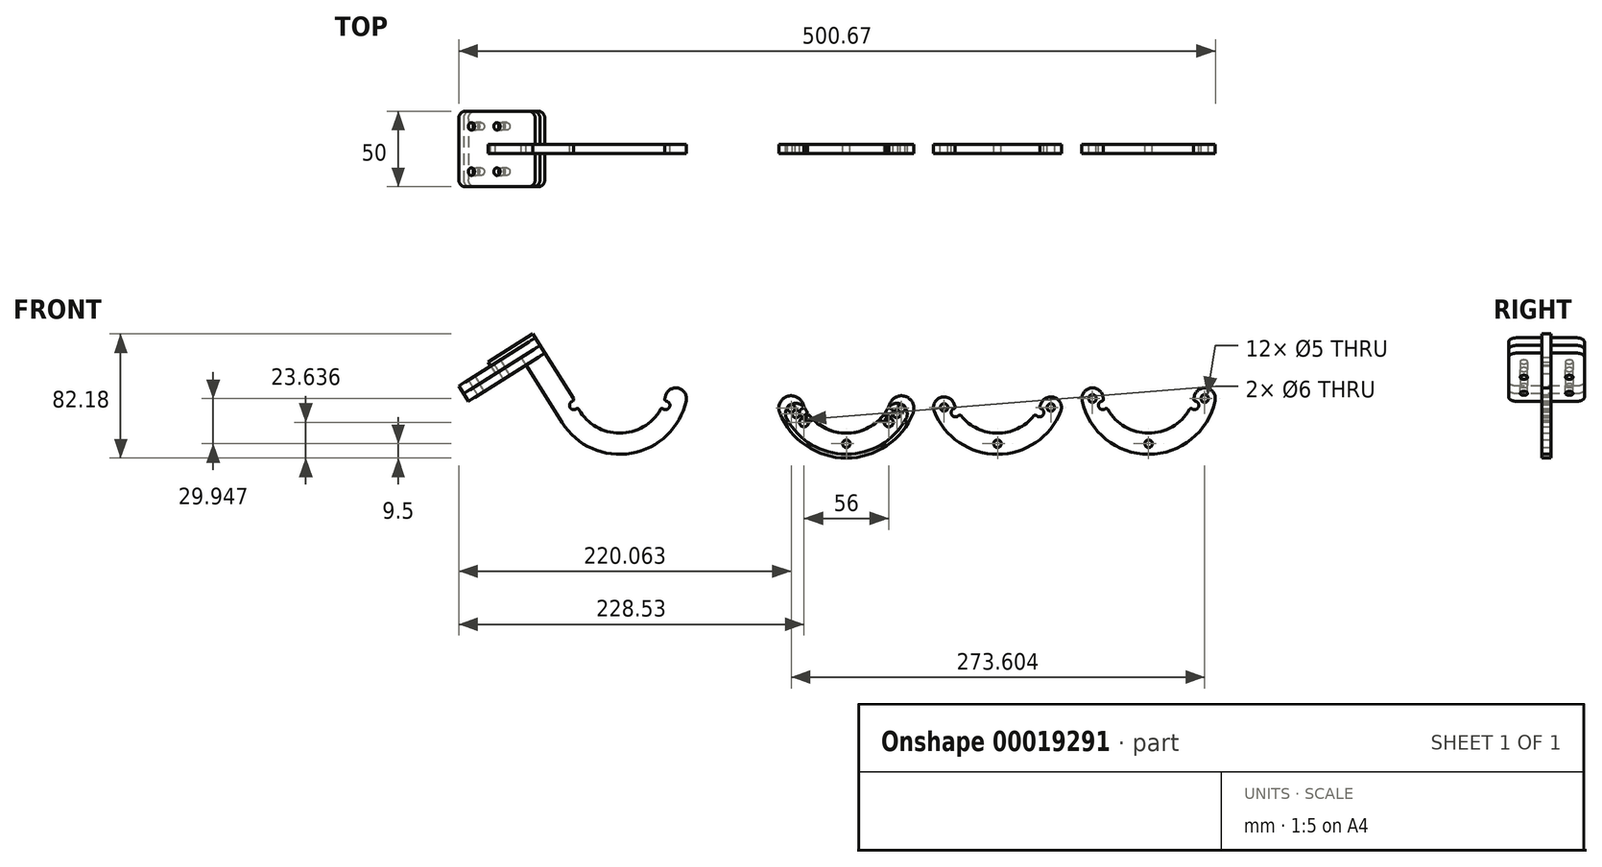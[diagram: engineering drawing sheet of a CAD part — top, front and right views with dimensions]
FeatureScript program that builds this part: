
annotation { "Feature Type Name" : "Feature", "Feature Type Description" : "" }
export const myFeature = defineFeature(function(context is Context, id is Id, definition is map)
    precondition{}
    {
        {
            var Q0;
            Q0=qCreatedBy(makeId("Front.planeOp"),FACE);
            var sketch = newSketch(context, id + "F0", { "sketchPlane" : qUnion([Q0])});
            skCircle(sketch, "E0", {"center": v(0, 0) * mm, "radius": 30 * mm, "construction": true});
            skArc(sketch, "E1", {"start": v(-25.2, -18.05) * mm, "mid": v(-27.55, -22.7) * mm, "end": v(-22.53, -21.3) * mm});
            skArc(sketch, "E2", {"start": v(-22.53, -21.3) * mm, "mid": v(0, -31) * mm, "end": v(22.53, -21.3) * mm});
            skArc(sketch, "E3.trimOffspring", {"start": v(25.2, -18.05) * mm, "mid": v(26.24, -16.5) * mm, "end": v(27.19, -14.9) * mm});
            skArc(sketch, "E4.trimOffspring", {"start": v(22.53, -21.3) * mm, "mid": v(27.55, -22.7) * mm, "end": v(25.2, -18.05) * mm});
            skLineSegment(sketch, "E5", {"start": v(0, -20.9) * mm, "end": v(0, 0) * mm, "construction": true});
            skArc(sketch, "E6.trimOffspring", {"start": v(-27.19, -14.9) * mm, "mid": v(-26.24, -16.5) * mm, "end": v(-25.2, -18.05) * mm});
            skLineSegment(sketch, "E7", {"start": v(-27.19, -14.9) * mm, "end": v(27.19, -14.9) * mm, "construction": true});
            skLineSegment(sketch, "E8", {"start": v(-25.35, -20.9) * mm, "end": v(25.35, -20.9) * mm, "construction": true});
            skArc(sketch, "E9", {"start": v(-39.47, -21.62) * mm, "mid": v(0, -45) * mm, "end": v(39.47, -21.62) * mm});
            skArc(sketch, "E10", {"start": v(-27.19, -14.9) * mm, "mid": v(-36.7, -12.12) * mm, "end": v(-39.47, -21.62) * mm});
            skArc(sketch, "E11.0.MirrorCS", {"start": v(27.19, -14.9) * mm, "mid": v(36.7, -12.12) * mm, "end": v(39.47, -21.62) * mm});
            skCircle(sketch, "E12", {"center": v(-33.33, -18.26) * mm, "radius": 2.5 * mm});
            skCircle(sketch, "E13", {"center": v(-33.33, -18.26) * mm, "radius": 4.5 * mm, "construction": true});
            skCircle(sketch, "E14.0.MirrorC", {"center": v(33.33, -18.26) * mm, "radius": 4.5 * mm, "construction": true});
            skCircle(sketch, "E14.1.MirrorC", {"center": v(33.33, -18.26) * mm, "radius": 2.5 * mm});
            skCircle(sketch, "E15", {"center": v(0, -38) * mm, "radius": 2.5 * mm});
            skCircle(sketch, "E16", {"center": v(0, -38) * mm, "radius": 4.5 * mm, "construction": true});
            skSolve(sketch);
        }
        {
            var Q0;
            Q0=qCreatedBy(makeId("Front.planeOp"),FACE);
            var sketch = newSketch(context, id + "F1", { "sketchPlane" : qUnion([Q0])});
            skCircle(sketch, "E17", {"center": v(100, 0) * mm, "radius": 30 * mm, "construction": true});
            skArc(sketch, "E18", {"start": v(72.66, -14.62) * mm, "mid": v(69.73, -18.93) * mm, "end": v(74.9, -18.19) * mm});
            skArc(sketch, "E19", {"start": v(74.9, -18.19) * mm, "mid": v(100, -31) * mm, "end": v(125.1, -18.19) * mm});
            skArc(sketch, "E20.trimOffspring", {"start": v(127.34, -14.62) * mm, "mid": v(128.12, -13.04) * mm, "end": v(128.82, -11.42) * mm});
            skArc(sketch, "E21.trimOffspring", {"start": v(125.1, -18.19) * mm, "mid": v(130.27, -18.93) * mm, "end": v(127.34, -14.62) * mm});
            skLineSegment(sketch, "E22", {"start": v(100, -17.42) * mm, "end": v(100, 0) * mm, "construction": true});
            skArc(sketch, "E23.trimOffspring", {"start": v(71.18, -11.42) * mm, "mid": v(71.88, -13.04) * mm, "end": v(72.66, -14.62) * mm});
            skLineSegment(sketch, "E24", {"start": v(71.18, -11.42) * mm, "end": v(128.82, -11.42) * mm, "construction": true});
            skLineSegment(sketch, "E25", {"start": v(72.15, -17.42) * mm, "end": v(127.85, -17.42) * mm, "construction": true});
            skArc(sketch, "E26", {"start": v(58.17, -16.58) * mm, "mid": v(100, -45) * mm, "end": v(141.83, -16.58) * mm});
            skArc(sketch, "E27", {"start": v(71.18, -11.42) * mm, "mid": v(62.1, -7.5) * mm, "end": v(58.17, -16.58) * mm});
            skArc(sketch, "E28.0.MirrorCS", {"start": v(128.82, -11.42) * mm, "mid": v(137.9, -7.5) * mm, "end": v(141.83, -16.58) * mm});
            skCircle(sketch, "E29", {"center": v(64.67, -14) * mm, "radius": 2.5 * mm});
            skCircle(sketch, "E30", {"center": v(64.67, -14) * mm, "radius": 4.5 * mm, "construction": true});
            skCircle(sketch, "E31.0.MirrorC", {"center": v(135.33, -14) * mm, "radius": 4.5 * mm, "construction": true});
            skCircle(sketch, "E31.1.MirrorC", {"center": v(135.33, -14) * mm, "radius": 2.5 * mm});
            skCircle(sketch, "E32", {"center": v(100, -38) * mm, "radius": 2.5 * mm});
            skCircle(sketch, "E33", {"center": v(100, -38) * mm, "radius": 4.5 * mm, "construction": true});
            skSolve(sketch);
        }
        {
            var Q0;
            Q0=qCreatedBy(makeId("Front.planeOp"),FACE);
            var sketch = newSketch(context, id + "F2", { "sketchPlane" : qUnion([Q0])});
            skCircle(sketch, "E34", {"center": v(200, 0) * mm, "radius": 30 * mm, "construction": true});
            skArc(sketch, "E35", {"start": v(170.62, -9.89) * mm, "mid": v(167.02, -13.66) * mm, "end": v(172.23, -13.78) * mm});
            skArc(sketch, "E36", {"start": v(172.23, -13.78) * mm, "mid": v(200, -31) * mm, "end": v(227.77, -13.78) * mm});
            skArc(sketch, "E37.trimOffspring", {"start": v(229.38, -9.89) * mm, "mid": v(229.88, -8.24) * mm, "end": v(230.3, -6.57) * mm});
            skArc(sketch, "E38.trimOffspring", {"start": v(227.77, -13.78) * mm, "mid": v(232.98, -13.66) * mm, "end": v(229.38, -9.89) * mm});
            skLineSegment(sketch, "E39", {"start": v(200, -12.57) * mm, "end": v(200, 0) * mm, "construction": true});
            skArc(sketch, "E40.trimOffspring", {"start": v(169.7, -6.57) * mm, "mid": v(170.12, -8.24) * mm, "end": v(170.62, -9.89) * mm});
            skLineSegment(sketch, "E41", {"start": v(169.7, -6.57) * mm, "end": v(230.3, -6.57) * mm, "construction": true});
            skLineSegment(sketch, "E42", {"start": v(169.65, -12.57) * mm, "end": v(230.35, -12.57) * mm, "construction": true});
            skArc(sketch, "E43", {"start": v(156.02, -9.54) * mm, "mid": v(200, -45) * mm, "end": v(243.98, -9.54) * mm});
            skArc(sketch, "E44", {"start": v(169.7, -6.57) * mm, "mid": v(161.38, -1.21) * mm, "end": v(156.02, -9.54) * mm});
            skArc(sketch, "E45.0.MirrorCS", {"start": v(230.3, -6.57) * mm, "mid": v(238.62, -1.21) * mm, "end": v(243.98, -9.54) * mm});
            skCircle(sketch, "E46", {"center": v(162.86, -8.05) * mm, "radius": 2.5 * mm});
            skCircle(sketch, "E47", {"center": v(162.86, -8.05) * mm, "radius": 4.5 * mm, "construction": true});
            skCircle(sketch, "E48.0.MirrorC", {"center": v(237.14, -8.05) * mm, "radius": 4.5 * mm, "construction": true});
            skCircle(sketch, "E48.1.MirrorC", {"center": v(237.14, -8.05) * mm, "radius": 2.5 * mm});
            skCircle(sketch, "E49", {"center": v(200, -38) * mm, "radius": 2.5 * mm});
            skCircle(sketch, "E50", {"center": v(200, -38) * mm, "radius": 4.5 * mm, "construction": true});
            skSolve(sketch);
        }
        {
            var Q0;
            Q0=qCreatedBy(makeId("Front.planeOp"),FACE);
            var sketch = newSketch(context, id + "F3", { "sketchPlane" : qUnion([Q0])});
            skCircle(sketch, "E51", {"center": v(-150, 0) * mm, "radius": 30 * mm, "construction": true});
            skArc(sketch, "E52", {"start": v(-179.38, -9.89) * mm, "mid": v(-182.98, -13.66) * mm, "end": v(-177.77, -13.78) * mm});
            skArc(sketch, "E53", {"start": v(-177.77, -13.78) * mm, "mid": v(-150, -31) * mm, "end": v(-122.23, -13.78) * mm});
            skArc(sketch, "E54.trimOffspring", {"start": v(-120.62, -9.89) * mm, "mid": v(-120.12, -8.24) * mm, "end": v(-119.7, -6.57) * mm});
            skArc(sketch, "E55.trimOffspring", {"start": v(-122.23, -13.78) * mm, "mid": v(-117.02, -13.66) * mm, "end": v(-120.62, -9.89) * mm});
            skLineSegment(sketch, "E56", {"start": v(-150, -12.57) * mm, "end": v(-150, 0) * mm, "construction": true});
            skArc(sketch, "E57.trimOffspring", {"start": v(-180.3, -6.57) * mm, "mid": v(-179.88, -8.24) * mm, "end": v(-179.38, -9.89) * mm});
            skLineSegment(sketch, "E58", {"start": v(-180.3, -6.57) * mm, "end": v(-119.7, -6.57) * mm, "construction": true});
            skLineSegment(sketch, "E59", {"start": v(-180.35, -12.57) * mm, "end": v(-119.65, -12.57) * mm, "construction": true});
            skArc(sketch, "E60", {"start": v(-193.98, -9.54) * mm, "mid": v(-150, -45) * mm, "end": v(-106.02, -9.54) * mm});
            skArc(sketch, "E61", {"start": v(-180.3, -6.57) * mm, "mid": v(-188.62, -1.21) * mm, "end": v(-193.98, -9.54) * mm, "construction": true});
            skArc(sketch, "E62.0.MirrorCS", {"start": v(-119.7, -6.57) * mm, "mid": v(-111.38, -1.21) * mm, "end": v(-106.02, -9.54) * mm});
            skCircle(sketch, "E63", {"center": v(-187.14, -8.05) * mm, "radius": 2.5 * mm, "construction": true});
            skCircle(sketch, "E64", {"center": v(-187.14, -8.05) * mm, "radius": 4.5 * mm, "construction": true});
            skCircle(sketch, "E65.0.MirrorC", {"center": v(-112.86, -8.05) * mm, "radius": 4.5 * mm, "construction": true});
            skCircle(sketch, "E65.1.MirrorC", {"center": v(-112.86, -8.05) * mm, "radius": 2.5 * mm, "construction": true});
            skCircle(sketch, "E66", {"center": v(-147.8, -37.94) * mm, "radius": 2.5 * mm, "construction": true});
            skCircle(sketch, "E67", {"center": v(-147.8, -37.94) * mm, "radius": 4.5 * mm, "construction": true});
            skLineSegment(sketch, "E68", {"start": v(-193.98, -9.54) * mm, "end": v(-203.94, 36.4) * mm, "construction": true});
            skLineSegment(sketch, "E69", {"start": v(-203.94, 36.4) * mm, "end": v(-190.26, 39.36) * mm, "construction": true});
            skLineSegment(sketch, "E70", {"start": v(-190.26, 39.36) * mm, "end": v(-180.3, -6.57) * mm, "construction": true});
            skLineSegment(sketch, "E71", {"start": v(-188.06, -24) * mm, "end": v(-220.07, 26.75) * mm});
            skLineSegment(sketch, "E72", {"start": v(-220.07, 26.75) * mm, "end": v(-207.49, 34.68) * mm});
            skLineSegment(sketch, "E73", {"start": v(-207.49, 34.68) * mm, "end": v(-179.38, -9.89) * mm});
            skLineSegment(sketch, "E74.bottom", {"start": v(-207.49, 34.68) * mm, "end": v(-236.98, 16.08) * mm});
            skLineSegment(sketch, "E74.top", {"start": v(-202.68, 27.07) * mm, "end": v(-232.18, 8.47) * mm});
            skLineSegment(sketch, "E74.left", {"start": v(-207.49, 34.68) * mm, "end": v(-202.68, 27.07) * mm});
            skLineSegment(sketch, "E74.right", {"start": v(-236.98, 16.08) * mm, "end": v(-232.18, 8.47) * mm});
            skSolve(sketch);
        }
        {
            var Q0;
            Q0=qSketchRegion(id+"F0",true);
            var Q1;
            Q1=qSketchRegion(id+"F1",true);
            var Q2;
            Q2=qSketchRegion(id+"F2",true);
            var Q3;
            Q3=qSketchRegion(id+"F3",true);
            extrude(context, id + "F4", {"entities" : qUnion([Q0, Q1, Q2, Q3]), "depth" : 6 * mm});
        }
        {
            var Q0;
            Q0=qCreatedBy(makeId("Front.planeOp"),FACE);
            var sketch = newSketch(context, id + "F5", { "sketchPlane" : qUnion([Q0])});
            skCircle(sketch, "E75", {"center": v(0, 0) * mm, "radius": 30 * mm, "construction": true});
            skArc(sketch, "E76", {"start": v(-27.39, -14.53) * mm, "mid": v(-30.55, -19.05) * mm, "end": v(-25.1, -18.2) * mm});
            skArc(sketch, "E77", {"start": v(-25.1, -18.2) * mm, "mid": v(0, -31) * mm, "end": v(25.1, -18.2) * mm});
            skArc(sketch, "E78.trimOffspring", {"start": v(27.39, -14.53) * mm, "mid": v(28.14, -13.02) * mm, "end": v(28.8, -11.46) * mm});
            skArc(sketch, "E79.trimOffspring", {"start": v(25.1, -18.2) * mm, "mid": v(30.55, -19.05) * mm, "end": v(27.39, -14.53) * mm});
            skLineSegment(sketch, "E80", {"start": v(0, -17.46) * mm, "end": v(0, 0) * mm, "construction": true});
            skArc(sketch, "E81.trimOffspring", {"start": v(-28.8, -11.46) * mm, "mid": v(-28.14, -13.02) * mm, "end": v(-27.39, -14.53) * mm});
            skLineSegment(sketch, "E82", {"start": v(-28.8, -11.46) * mm, "end": v(28.8, -11.46) * mm, "construction": true});
            skLineSegment(sketch, "E83", {"start": v(-28, -17.46) * mm, "end": v(28, -17.46) * mm, "construction": true});
            skArc(sketch, "E84", {"start": v(-44.13, -17.57) * mm, "mid": v(0, -47.5) * mm, "end": v(44.13, -17.57) * mm});
            skArc(sketch, "E85", {"start": v(-28.8, -11.46) * mm, "mid": v(-39.52, -6.85) * mm, "end": v(-44.13, -17.57) * mm});
            skArc(sketch, "E86.0.MirrorCS", {"start": v(28.8, -11.46) * mm, "mid": v(39.52, -6.85) * mm, "end": v(44.13, -17.57) * mm});
            skCircle(sketch, "E87", {"center": v(-36.47, -14.52) * mm, "radius": 2.5 * mm});
            skCircle(sketch, "E88", {"center": v(-36.47, -14.52) * mm, "radius": 4.5 * mm, "construction": true});
            skCircle(sketch, "E89.0.MirrorC", {"center": v(36.47, -14.52) * mm, "radius": 4.5 * mm, "construction": true});
            skCircle(sketch, "E89.1.MirrorC", {"center": v(36.47, -14.52) * mm, "radius": 2.5 * mm});
            skCircle(sketch, "E90", {"center": v(0, -38) * mm, "radius": 2.5 * mm});
            skCircle(sketch, "E91", {"center": v(0, -38) * mm, "radius": 4.5 * mm, "construction": true});
            skCircle(sketch, "E92", {"center": v(-28, -23.86) * mm, "radius": 3 * mm});
            skCircle(sketch, "E93.2.MirrorC", {"center": v(28, -23.86) * mm, "radius": 3 * mm});
            skSolve(sketch);
        }
        {
            var Q0;
            {var subQ8=sQuery(id+"F5.wireOp",EDGE,"E77");Q0=makeQuery(id+"F5.imprint","IMPRINT",FACE,{"disambiguationData":[TD([[makeQuery(id+"F5.imprint","IMPRINT",EDGE,{"derivedFrom":subQ8}),-1.0]])]});}
            extrude(context, id + "F6", {"entities" : qUnion([Q0]), "depth" : 6 * mm});
        }
        {
            var Q0;
            Q0=makeQuery(id+"F4.opExtrude","SWEPT_EDGE",EDGE,{"disambiguationData":[OSD([sQuery(id+"F8bxkwO3vdnG2yd_0.wireOp",EDGE,"31eb92c2-16fb-4c42-9b8d-966ca1aeed332"),sQuery(id+"F8bxkwO3vdnG2yd_0.wireOp",EDGE,"2c9158f4-900c-449d-a254-1914823e743f2")])]});
            var Q1;
            Q1=makeQuery(id+"F4.opExtrude","SWEPT_EDGE",EDGE,{"disambiguationData":[OSD([sQuery(id+"F8bxkwO3vdnG2yd_0.wireOp",EDGE,"eb435ce6-0262-44dd-993c-7a231c0c74591"),sQuery(id+"F8bxkwO3vdnG2yd_0.wireOp",EDGE,"2c9158f4-900c-449d-a254-1914823e743f2")])]});
            var Q2;
            Q2=makeQuery(id+"F4.opExtrude","SWEPT_EDGE",EDGE,{"disambiguationData":[OSD([sQuery(id+"F8bxkwO3vdnG2yd_0.wireOp",EDGE,"eb435ce6-0262-44dd-993c-7a231c0c74591"),sQuery(id+"F8bxkwO3vdnG2yd_0.wireOp",EDGE,"3728cfd9-2cba-40b4-b20c-720c0a8e45b42")])]});
            var Q3;
            Q3=makeQuery(id+"F4.opExtrude","SWEPT_EDGE",EDGE,{"disambiguationData":[OSD([sQuery(id+"F8bxkwO3vdnG2yd_0.wireOp",EDGE,"8c1682ca-4a2a-44f7-86e0-5e973af3ea3f1"),sQuery(id+"F8bxkwO3vdnG2yd_0.wireOp",EDGE,"3728cfd9-2cba-40b4-b20c-720c0a8e45b42")])]});
            var Q4;
            Q4=makeQuery(id+"F4.opExtrude","SWEPT_EDGE",EDGE,{"disambiguationData":[OSD([sQuery(id+"F0.wireOp",EDGE,"E1"),sQuery(id+"F0.wireOp",EDGE,"E6.trimOffspring")])]});
            var Q5;
            Q5=makeQuery(id+"F4.opExtrude","SWEPT_EDGE",EDGE,{"disambiguationData":[OSD([sQuery(id+"F0.wireOp",EDGE,"E1"),sQuery(id+"F0.wireOp",EDGE,"E2")])]});
            var Q6;
            Q6=makeQuery(id+"F4.opExtrude","SWEPT_EDGE",EDGE,{"disambiguationData":[OSD([sQuery(id+"F0.wireOp",EDGE,"E3.trimOffspring"),sQuery(id+"F0.wireOp",EDGE,"E4.trimOffspring")])]});
            var Q7;
            Q7=makeQuery(id+"F4.opExtrude","SWEPT_EDGE",EDGE,{"disambiguationData":[OSD([sQuery(id+"F0.wireOp",EDGE,"E2"),sQuery(id+"F0.wireOp",EDGE,"E4.trimOffspring")])]});
            var Q8;
            Q8=makeQuery(id+"F6.opExtrude","SWEPT_EDGE",EDGE,{"disambiguationData":[OSD([sQuery(id+"F5.wireOp",EDGE,"E76"),sQuery(id+"F5.wireOp",EDGE,"E81.trimOffspring")])]});
            var Q9;
            Q9=makeQuery(id+"F6.opExtrude","SWEPT_EDGE",EDGE,{"disambiguationData":[OSD([sQuery(id+"F5.wireOp",EDGE,"E76"),sQuery(id+"F5.wireOp",EDGE,"E77")])]});
            var Q10;
            Q10=makeQuery(id+"F6.opExtrude","SWEPT_EDGE",EDGE,{"disambiguationData":[OSD([sQuery(id+"F5.wireOp",EDGE,"E78.trimOffspring"),sQuery(id+"F5.wireOp",EDGE,"E79.trimOffspring")])]});
            var Q11;
            Q11=makeQuery(id+"F6.opExtrude","SWEPT_EDGE",EDGE,{"disambiguationData":[OSD([sQuery(id+"F5.wireOp",EDGE,"E77"),sQuery(id+"F5.wireOp",EDGE,"E79.trimOffspring")])]});
            var Q12;
            Q12=makeQuery(id+"F4.opExtrude","SWEPT_EDGE",EDGE,{"disambiguationData":[OSD([sQuery(id+"F1.wireOp",EDGE,"E18"),sQuery(id+"F1.wireOp",EDGE,"E23.trimOffspring")])]});
            var Q13;
            Q13=makeQuery(id+"F4.opExtrude","SWEPT_EDGE",EDGE,{"disambiguationData":[OSD([sQuery(id+"F1.wireOp",EDGE,"E18"),sQuery(id+"F1.wireOp",EDGE,"E19")])]});
            var Q14;
            Q14=makeQuery(id+"F4.opExtrude","SWEPT_EDGE",EDGE,{"disambiguationData":[OSD([sQuery(id+"F1.wireOp",EDGE,"E20.trimOffspring"),sQuery(id+"F1.wireOp",EDGE,"E21.trimOffspring")])]});
            var Q15;
            Q15=makeQuery(id+"F4.opExtrude","SWEPT_EDGE",EDGE,{"disambiguationData":[OSD([sQuery(id+"F1.wireOp",EDGE,"E19"),sQuery(id+"F1.wireOp",EDGE,"E21.trimOffspring")])]});
            var Q16;
            Q16=makeQuery(id+"F4.opExtrude","SWEPT_EDGE",EDGE,{"disambiguationData":[OSD([sQuery(id+"F2.wireOp",EDGE,"E35"),sQuery(id+"F2.wireOp",EDGE,"E40.trimOffspring")])]});
            var Q17;
            Q17=makeQuery(id+"F4.opExtrude","SWEPT_EDGE",EDGE,{"disambiguationData":[OSD([sQuery(id+"F2.wireOp",EDGE,"E35"),sQuery(id+"F2.wireOp",EDGE,"E36")])]});
            var Q18;
            Q18=makeQuery(id+"F4.opExtrude","SWEPT_EDGE",EDGE,{"disambiguationData":[OSD([sQuery(id+"F2.wireOp",EDGE,"E37.trimOffspring"),sQuery(id+"F2.wireOp",EDGE,"E38.trimOffspring")])]});
            var Q19;
            Q19=makeQuery(id+"F4.opExtrude","SWEPT_EDGE",EDGE,{"disambiguationData":[OSD([sQuery(id+"F2.wireOp",EDGE,"E36"),sQuery(id+"F2.wireOp",EDGE,"E38.trimOffspring")])]});
            var Q20;
            Q20=makeQuery(id+"F4.opExtrude","SWEPT_EDGE",EDGE,{"disambiguationData":[OSD([sQuery(id+"F3.wireOp",EDGE,"E52"),sQuery(id+"F3.wireOp",EDGE,"E57.trimOffspring")])]});
            var Q21;
            Q21=makeQuery(id+"F4.opExtrude","SWEPT_EDGE",EDGE,{"disambiguationData":[OSD([sQuery(id+"F3.wireOp",EDGE,"E52"),sQuery(id+"F3.wireOp",EDGE,"E53")])]});
            var Q22;
            Q22=makeQuery(id+"F4.opExtrude","SWEPT_EDGE",EDGE,{"disambiguationData":[OSD([sQuery(id+"F3.wireOp",EDGE,"E53"),sQuery(id+"F3.wireOp",EDGE,"E55.trimOffspring")])]});
            var Q23;
            Q23=makeQuery(id+"F4.opExtrude","SWEPT_EDGE",EDGE,{"disambiguationData":[OSD([sQuery(id+"F3.wireOp",EDGE,"E54.trimOffspring"),sQuery(id+"F3.wireOp",EDGE,"E55.trimOffspring")])]});
            fillet(context, id + "F7", {"entities" : qUnion([Q0, Q1, Q2, Q3, Q4, Q5, Q6, Q7, Q8, Q9, Q10, Q11, Q12, Q13, Q14, Q15, Q16, Q17, Q18, Q19, Q20, Q21, Q22, Q23]), "radius" : 1.25 * mm, "tangentPropagation" : true, "allowEdgeOverflow" : false});
        }
        {
            var Q0;
            Q0=makeQuery(id+"F4.opExtrude","SWEPT_FACE",FACE,{"disambiguationData":[OSD([sQuery(id+"F3.wireOp",EDGE,"E74.top")])]});
            var sketch = newSketch(context, id + "F8", { "sketchPlane" : qUnion([Q0])});
            skLineSegment(sketch, "E94.bottom", {"start": v(-157, -22) * mm, "end": v(-216.88, -22) * mm});
            skLineSegment(sketch, "E94.top", {"start": v(-157, 28) * mm, "end": v(-216.88, 28) * mm});
            skLineSegment(sketch, "E94.left", {"start": v(-157, -22) * mm, "end": v(-157, 28) * mm});
            skLineSegment(sketch, "E94.right", {"start": v(-216.88, -22) * mm, "end": v(-216.88, 28) * mm});
            skLineSegment(sketch, "E95", {"start": v(-157, 3) * mm, "end": v(-216.88, 3) * mm, "construction": true});
            skPoint(sketch, "E96", {"position": v(-191.88, 3) * mm});
            skLineSegment(sketch, "E97.bottom", {"start": v(-157, 0) * mm, "end": v(-171.88, 0) * mm});
            skLineSegment(sketch, "E97.top", {"start": v(-157, 6) * mm, "end": v(-171.88, 6) * mm});
            skLineSegment(sketch, "E97.left", {"start": v(-157, 0) * mm, "end": v(-157, 6) * mm});
            skLineSegment(sketch, "E97.right", {"start": v(-171.88, 0) * mm, "end": v(-171.88, 6) * mm});
            skCircle(sketch, "E98", {"center": v(-186.88, -12) * mm, "radius": 2.5 * mm});
            skCircle(sketch, "E99", {"center": v(-186.88, 18) * mm, "radius": 2.5 * mm});
            skLineSegment(sketch, "E100", {"start": v(-176.88, -22) * mm, "end": v(-176.88, 28) * mm, "construction": true});
            skCircle(sketch, "E101", {"center": v(-206.88, -12) * mm, "radius": 2.5 * mm});
            skCircle(sketch, "E102", {"center": v(-206.88, 18) * mm, "radius": 2.5 * mm});
            skSolve(sketch);
        }
        {
            var Q0;
            Q0=makeQuery(id+"F8.imprint","IMPRINT",FACE,{"disambiguationData":[TD([[makeQuery(id+"F8.imprint","IMPRINT",EDGE,{"derivedFrom":sQuery(id+"F8.wireOp",EDGE,"E97.right")}),-1.0]])]});
            var Q1;
            {var subQ6=sQuery(id+"F8.wireOp",EDGE,"E94.bottom");Q1=makeQuery(id+"F8.imprint","IMPRINT",FACE,{"disambiguationData":[TD([[makeQuery(id+"F8.imprint","IMPRINT",EDGE,{"derivedFrom":subQ6}),-1.0]])]});}
            extrude(context, id + "F9", {"entities" : qUnion([Q0, Q1]), "depth" : 6 * mm});
        }
        {
            var Q0;
            Q0=makeQuery(id+"F9.opExtrude","CAP_FACE",FACE,{"disambiguationData":[OSD([sQuery(id+"F8.wireOp",EDGE,"E94.bottom"),sQuery(id+"F8.wireOp",EDGE,"E94.top"),sQuery(id+"F8.wireOp",EDGE,"E94.left"),sQuery(id+"F8.wireOp",EDGE,"E94.right"),sQuery(id+"F8.wireOp",EDGE,"E97.bottom"),sQuery(id+"F8.wireOp",EDGE,"E97.top"),sQuery(id+"F8.wireOp",EDGE,"E97.right"),sQuery(id+"F8.wireOp",EDGE,"E98"),sQuery(id+"F8.wireOp",EDGE,"E99"),sQuery(id+"F8.wireOp",EDGE,"E101"),sQuery(id+"F8.wireOp",EDGE,"E102")])],"isStart":true});
            var sketch = newSketch(context, id + "F10", { "sketchPlane" : qUnion([Q0])});
            skLineSegment(sketch, "E103.bottom", {"start": v(-216.88, 22) * mm, "end": v(-157, 22) * mm});
            skLineSegment(sketch, "E103.top", {"start": v(-216.88, -28) * mm, "end": v(-157, -28) * mm});
            skLineSegment(sketch, "E103.left", {"start": v(-216.88, 22) * mm, "end": v(-216.88, -28) * mm});
            skLineSegment(sketch, "E103.right", {"start": v(-157, 22) * mm, "end": v(-157, -28) * mm});
            skCircle(sketch, "E104.1", {"center": v(-186.88, 12) * mm, "radius": 2.5 * mm});
            skCircle(sketch, "E104.2", {"center": v(-206.88, 12) * mm, "radius": 2.5 * mm});
            skCircle(sketch, "E104.3", {"center": v(-206.88, -18) * mm, "radius": 2.5 * mm});
            skCircle(sketch, "E104.4", {"center": v(-186.88, -18) * mm, "radius": 2.5 * mm});
            skLineSegment(sketch, "E105.0", {"start": v(-157, -6) * mm, "end": v(-157, 0) * mm});
            skLineSegment(sketch, "E105.1", {"start": v(-157, 0) * mm, "end": v(-191.88, 0) * mm});
            skLineSegment(sketch, "E105.2", {"start": v(-157, -6) * mm, "end": v(-191.88, -6) * mm});
            skLineSegment(sketch, "E105.3", {"start": v(-191.88, -6) * mm, "end": v(-191.88, 0) * mm});
            skSolve(sketch);
        }
        {
            var Q0;
            {var subQ11=sQuery(id+"F10.wireOp",EDGE,"E103.bottom");Q0=makeQuery(id+"F10.imprint","IMPRINT",FACE,{"disambiguationData":[TD([[makeQuery(id+"F10.imprint","IMPRINT",EDGE,{"derivedFrom":subQ11}),1.0]])]});}
            extrude(context, id + "F11", {"entities" : qUnion([Q0]), "depth" : 6 * mm});
        }
        {
            var Q0;
            Q0=makeQuery(id+"F4.opExtrude","SWEPT_EDGE",EDGE,{"disambiguationData":[OSD([sQuery(id+"F3.wireOp",EDGE,"8eaa4e57-1036-4e1c-8d5c-6fa1912e2a20"),sQuery(id+"F3.wireOp",EDGE,"e638c48f-3428-4f90-a1b5-2cb3346b7ef3")])]});
            var Q1;
            Q1=makeQuery(id+"F9.opExtrude","SWEPT_EDGE",EDGE,{"disambiguationData":[OSD([sQuery(id+"F8.wireOp",EDGE,"E94.top"),sQuery(id+"F8.wireOp",EDGE,"E94.left")])]});
            var Q2;
            Q2=makeQuery(id+"F9.opExtrude","SWEPT_EDGE",EDGE,{"disambiguationData":[OSD([sQuery(id+"F8.wireOp",EDGE,"E94.top"),sQuery(id+"F8.wireOp",EDGE,"E94.right")])]});
            var Q3;
            Q3=makeQuery(id+"F9.opExtrude","SWEPT_EDGE",EDGE,{"disambiguationData":[OSD([sQuery(id+"F8.wireOp",EDGE,"E94.bottom"),sQuery(id+"F8.wireOp",EDGE,"E94.right")])]});
            var Q4;
            Q4=makeQuery(id+"F9.opExtrude","SWEPT_EDGE",EDGE,{"disambiguationData":[OSD([sQuery(id+"F8.wireOp",EDGE,"E94.bottom"),sQuery(id+"F8.wireOp",EDGE,"E94.left")])]});
            var Q5;
            Q5=makeQuery(id+"F11.opExtrude","SWEPT_EDGE",EDGE,{"disambiguationData":[OSD([sQuery(id+"F10.wireOp",EDGE,"E103.top"),sQuery(id+"F10.wireOp",EDGE,"E103.left")])]});
            var Q6;
            Q6=makeQuery(id+"F11.opExtrude","SWEPT_EDGE",EDGE,{"disambiguationData":[OSD([sQuery(id+"F10.wireOp",EDGE,"E103.bottom"),sQuery(id+"F10.wireOp",EDGE,"E103.left")])]});
            var Q7;
            Q7=makeQuery(id+"F11.opExtrude","SWEPT_EDGE",EDGE,{"disambiguationData":[OSD([sQuery(id+"F10.wireOp",EDGE,"E103.top"),sQuery(id+"F10.wireOp",EDGE,"E103.right")])]});
            var Q8;
            Q8=makeQuery(id+"F11.opExtrude","SWEPT_EDGE",EDGE,{"disambiguationData":[OSD([sQuery(id+"F10.wireOp",EDGE,"E103.bottom"),sQuery(id+"F10.wireOp",EDGE,"E103.right")])]});
            fillet(context, id + "F12", {"entities" : qUnion([Q0, Q1, Q2, Q3, Q4, Q5, Q6, Q7, Q8]), "radius" : 5 * mm, "tangentPropagation" : true, "allowEdgeOverflow" : false});
        }
    });
